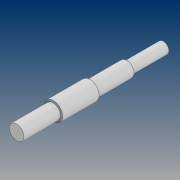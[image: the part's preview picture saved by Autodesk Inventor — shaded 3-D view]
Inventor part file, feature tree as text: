
AUTODESK INVENTOR PART (.ipt)
format: ipt  version: 2021 (Build 250183000, 183)  size: 92,672 bytes
history: native  units: mm
features: revolve x1, sketch x1
ambient origin geometry x8: Origin, YZ Plane, XZ Plane, XY Plane, X Axis, Y Axis, Z Axis, Center Point
bodies: Solid1 (feature_tree)
feature tree (2):
  revolve  "Revolution1"  [1 undecoded]
  sketch  "Sketch1"  dims[d0=3.0mm d1=80.0mm d2=60.0mm d3=20.0mm d4=4.0mm d5=5.0mm d6=90.0deg]
note: 1 required parameter value undecoded (feature->parameter linkage not recoverable at this tier; creation-order binding heuristic only, values carry confidence <= 0.55)
